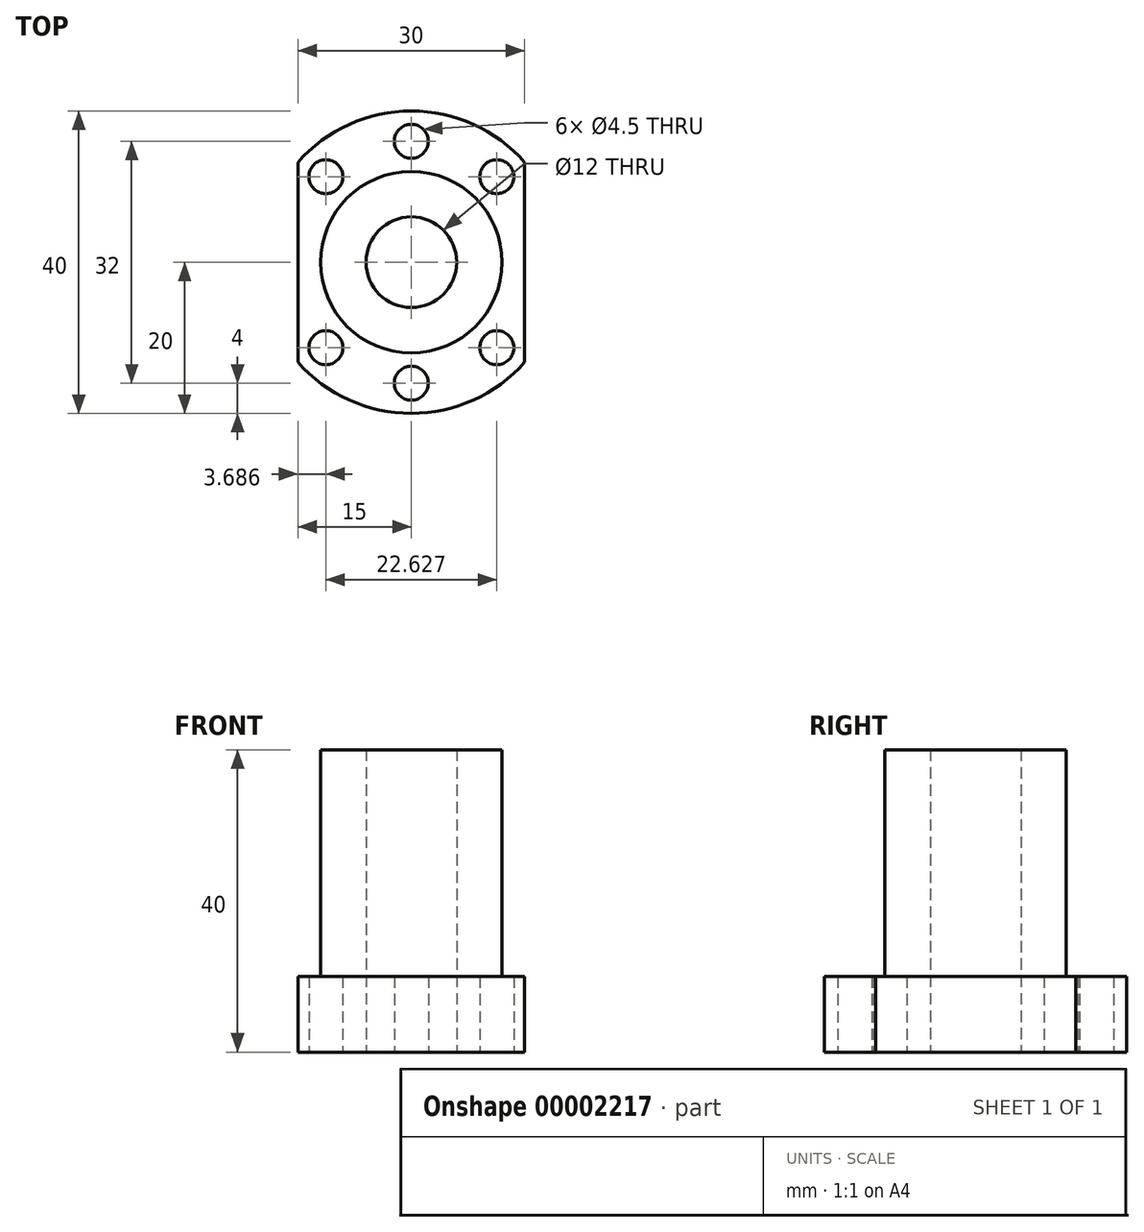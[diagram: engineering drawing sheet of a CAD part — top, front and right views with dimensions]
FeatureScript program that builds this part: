
annotation { "Feature Type Name" : "Feature", "Feature Type Description" : "" }
export const myFeature = defineFeature(function(context is Context, id is Id, definition is map)
    precondition{}
    {
        {
            var Q0;
            Q0=qCreatedBy(makeId("Top.planeOp"),FACE);
            var sketch = newSketch(context, id + "F0", { "sketchPlane" : qUnion([Q0])});
            skArc(sketch, "E0", {"start": v(-15, -13.23) * mm, "mid": v(0, -20) * mm, "end": v(15, -13.23) * mm});
            skLineSegment(sketch, "E1.rect.left", {"start": v(-15, 13.23) * mm, "end": v(-15, -13.23) * mm});
            skLineSegment(sketch, "E1.rect.right", {"start": v(15, 13.23) * mm, "end": v(15, -13.23) * mm});
            skPoint(sketch, "E1.rect.top.start.orphan", {"position": v(-15, -32.41) * mm});
            skPoint(sketch, "E2.orphan", {"position": v(15, -32.41) * mm});
            skArc(sketch, "E3.trimOffspring", {"start": v(15, 13.23) * mm, "mid": v(0, 20) * mm, "end": v(-15, 13.23) * mm});
            skPoint(sketch, "E1.rect.bottom.start.orphan", {"position": v(-15, 32.41) * mm});
            skPoint(sketch, "E4.orphan", {"position": v(15, 32.41) * mm});
            skCircle(sketch, "E5", {"center": v(0, 0) * mm, "radius": 16 * mm, "construction": true});
            skCircle(sketch, "E6", {"center": v(0, 0) * mm, "radius": 6 * mm});
            skCircle(sketch, "E7", {"center": v(0, 16) * mm, "radius": 2.25 * mm});
            skCircle(sketch, "E8", {"center": v(11.31, 11.31) * mm, "radius": 2.25 * mm});
            skCircle(sketch, "E9", {"center": v(-11.31, 11.31) * mm, "radius": 2.25 * mm});
            skLineSegment(sketch, "E10", {"start": v(0, 0) * mm, "end": v(-31.3, 0) * mm, "construction": true});
            skLineSegment(sketch, "E11", {"start": v(0, 0) * mm, "end": v(-29.04, 29.04) * mm, "construction": true});
            skLineSegment(sketch, "E12", {"start": v(0, 0) * mm, "end": v(25.68, 25.68) * mm, "construction": true});
            skCircle(sketch, "E13.0.MirrorC", {"center": v(11.31, -11.31) * mm, "radius": 2.25 * mm});
            skCircle(sketch, "E13.1.MirrorC", {"center": v(0, -16) * mm, "radius": 2.25 * mm});
            skCircle(sketch, "E13.2.MirrorC", {"center": v(-11.31, -11.31) * mm, "radius": 2.25 * mm});
            skSolve(sketch);
        }
        {
            var Q0;
            Q0 = qSketchRegion(id + "F0", true);
            extrude(context, id + "F1", {"entities" : qUnion([Q0]), "depth" : 40 * mm});
        }
        {
            var Q0;
            Q0=makeQuery(id+"F1.opExtrude","CAP_FACE",FACE,{"disambiguationData":[OSD([sQuery(id+"F0.wireOp",EDGE,"E0"),sQuery(id+"F0.wireOp",EDGE,"E1.rect.left"),sQuery(id+"F0.wireOp",EDGE,"E1.rect.right"),sQuery(id+"F0.wireOp",EDGE,"E3.trimOffspring"),sQuery(id+"F0.wireOp",EDGE,"E6"),sQuery(id+"F0.wireOp",EDGE,"E7"),sQuery(id+"F0.wireOp",EDGE,"E8"),sQuery(id+"F0.wireOp",EDGE,"E9"),sQuery(id+"F0.wireOp",EDGE,"E13.0.MirrorC"),sQuery(id+"F0.wireOp",EDGE,"E13.1.MirrorC"),sQuery(id+"F0.wireOp",EDGE,"E13.2.MirrorC")])],"isStart":false});
            var sketch = newSketch(context, id + "F2", { "sketchPlane" : qUnion([Q0])});
            skCircle(sketch, "E14", {"center": v(0, 0) * mm, "radius": 12 * mm});
            skCircle(sketch, "E15", {"center": v(0, 0) * mm, "radius": 27.62 * mm});
            skSolve(sketch);
        }
        {
            var Q0;
            Q0=makeQuery(id+"F2.imprint","IMPRINT",FACE,{"disambiguationData":[TD([[makeQuery(id+"F2.imprint","IMPRINT",EDGE,{"derivedFrom":sQuery(id+"F2.wireOp",EDGE,"E15")}),1.0]])]});
            var Q1;
            Q1=makeQuery(id+"F2.imprint","IMPRINT",FACE,{"disambiguationData":[TD([[makeQuery(id+"F2.imprint","IMPRINT",EDGE,{"derivedFrom":makeQuery(id+"F1.opExtrude","CAP_EDGE",EDGE,{"disambiguationData":[OSD([sQuery(id+"F0.wireOp",EDGE,"E6")])],"isStart":false})}),1.0]])]});
            var Q2;
            Q2=makeQuery(id+"F2.imprint","IMPRINT",FACE,{"disambiguationData":[TD([[makeQuery(id+"F2.imprint","IMPRINT",EDGE,{"derivedFrom":makeQuery(id+"F1.opExtrude","CAP_EDGE",EDGE,{"disambiguationData":[OSD([sQuery(id+"F0.wireOp",EDGE,"E7")])],"isStart":false})}),1.0]])]});
            var Q3;
            Q3=makeQuery(id+"F2.imprint","IMPRINT",FACE,{"disambiguationData":[TD([[makeQuery(id+"F2.imprint","IMPRINT",EDGE,{"derivedFrom":makeQuery(id+"F1.opExtrude","CAP_EDGE",EDGE,{"disambiguationData":[OSD([sQuery(id+"F0.wireOp",EDGE,"E8")])],"isStart":false})}),1.0]])]});
            var Q4;
            Q4=makeQuery(id+"F2.imprint","IMPRINT",FACE,{"disambiguationData":[TD([[makeQuery(id+"F2.imprint","IMPRINT",EDGE,{"derivedFrom":makeQuery(id+"F1.opExtrude","CAP_EDGE",EDGE,{"disambiguationData":[OSD([sQuery(id+"F0.wireOp",EDGE,"E9")])],"isStart":false})}),1.0]])]});
            var Q5;
            Q5=makeQuery(id+"F2.imprint","IMPRINT",FACE,{"disambiguationData":[TD([[makeQuery(id+"F2.imprint","IMPRINT",EDGE,{"derivedFrom":makeQuery(id+"F1.opExtrude","CAP_EDGE",EDGE,{"disambiguationData":[OSD([sQuery(id+"F0.wireOp",EDGE,"E13.0.MirrorC")])],"isStart":false})}),-1.0]])]});
            var Q6;
            Q6=makeQuery(id+"F2.imprint","IMPRINT",FACE,{"disambiguationData":[TD([[makeQuery(id+"F2.imprint","IMPRINT",EDGE,{"derivedFrom":makeQuery(id+"F1.opExtrude","CAP_EDGE",EDGE,{"disambiguationData":[OSD([sQuery(id+"F0.wireOp",EDGE,"E13.1.MirrorC")])],"isStart":false})}),-1.0]])]});
            var Q7;
            Q7=makeQuery(id+"F2.imprint","IMPRINT",FACE,{"disambiguationData":[TD([[makeQuery(id+"F2.imprint","IMPRINT",EDGE,{"derivedFrom":makeQuery(id+"F1.opExtrude","CAP_EDGE",EDGE,{"disambiguationData":[OSD([sQuery(id+"F0.wireOp",EDGE,"E13.2.MirrorC")])],"isStart":false})}),-1.0]])]});
            var Q8;
            Q8=makeQuery(id+"F2.imprint","IMPRINT",FACE,{"disambiguationData":[TD([[makeQuery(id+"F2.imprint","IMPRINT",EDGE,{"derivedFrom":sQuery(id+"F2.wireOp",EDGE,"E14")}),-1.0]])]});
            extrude(context, id + "F3", {"entities" : qUnion([Q0, Q1, Q2, Q3, Q4, Q5, Q6, Q7, Q8]), "operationType" : NewBodyOperationType.REMOVE, "oppositeDirection" : true, "depth" : 30 * mm});
        }
    });
